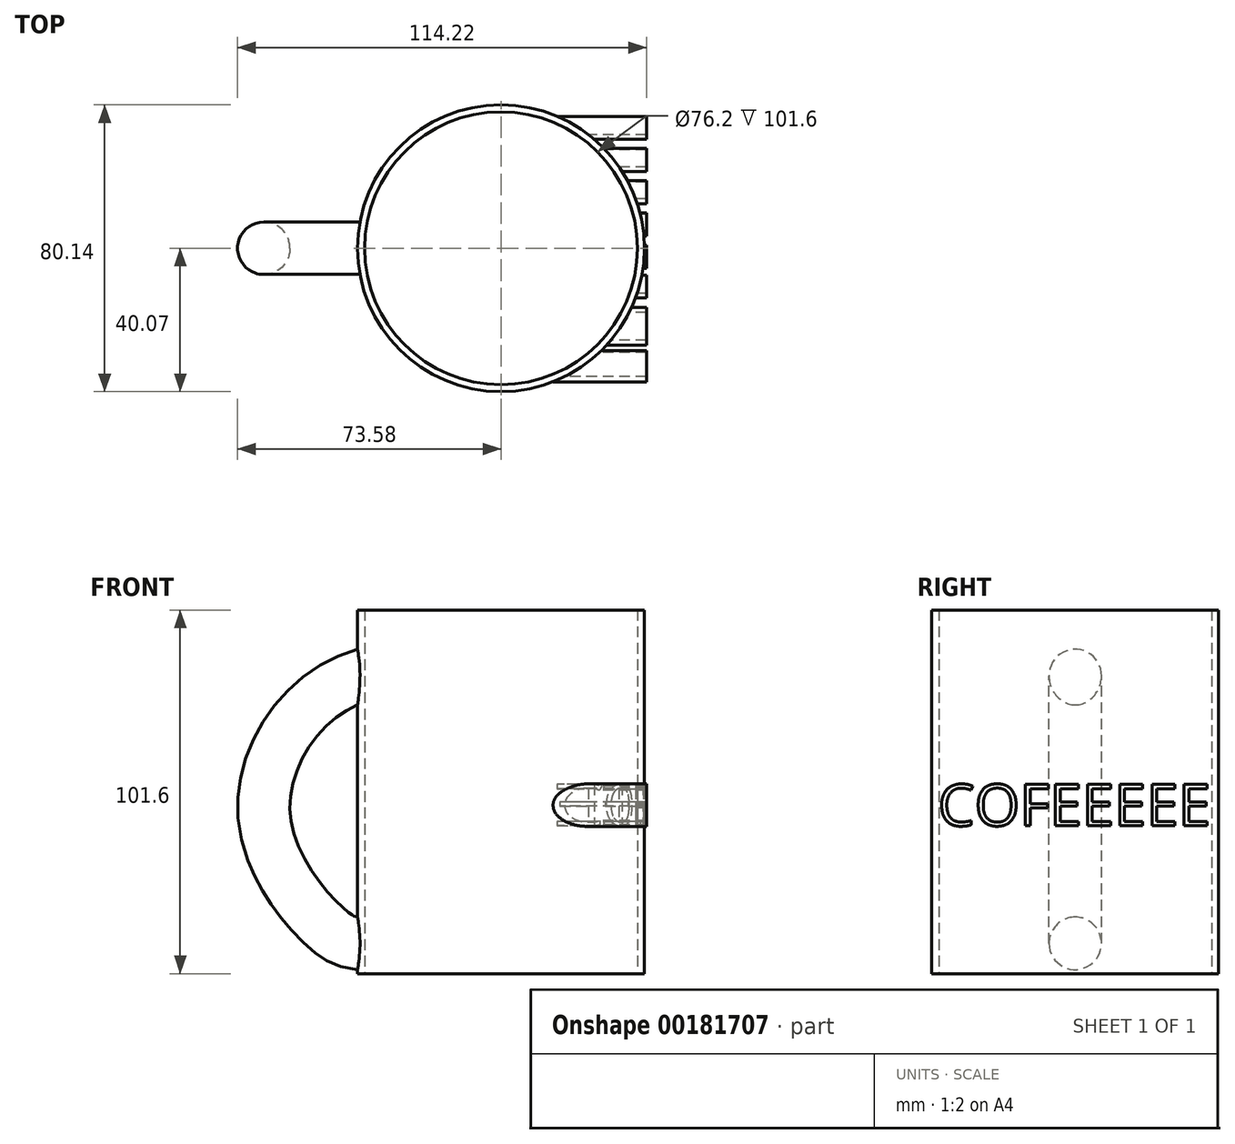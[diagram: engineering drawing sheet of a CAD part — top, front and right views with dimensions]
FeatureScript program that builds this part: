
annotation { "Feature Type Name" : "Feature", "Feature Type Description" : "" }
export const myFeature = defineFeature(function(context is Context, id is Id, definition is map)
    precondition{}
    {
        {
            var Q0;
            Q0=qCreatedBy(makeId("Top.planeOp"),FACE);
            var sketch = newSketch(context, id + "F0", { "sketchPlane" : qUnion([Q0])});
            skCircle(sketch, "E0", {"center": v(0, 0) * mm, "radius": 40.07 * mm});
            skSolve(sketch);
        }
        {
            var Q0;
            Q0 = qSketchRegion(id + "F0", true);
            extrude(context, id + "F1", {"entities" : qUnion([Q0]), "depth" : 101.6 * mm});
        }
        {
            var Q0;
            Q0=qCreatedBy(makeId("Right.planeOp"),FACE);
            var sketch = newSketch(context, id + "F2", { "sketchPlane" : qUnion([Q0])});
            skCircle(sketch, "E1", {"center": v(0, 84.76) * mm, "radius": 7.33 * mm});
            skSolve(sketch);
        }
        {
            var Q0;
            Q0=qCreatedBy(makeId("Front.planeOp"),FACE);
            var sketch = newSketch(context, id + "F3", { "sketchPlane" : qUnion([Q0])});
            skFitSpline(sketch, "E2", {"points": [v(0, 84.72) * mm, v(-47.14, 79.6) * mm, v(-66, 42.7) * mm, v(-47.14, 11.45) * mm, v(-9.6, 9.51) * mm], "startDerivative": vector(-191.11, 15.43) * mm, "endDerivative": vector(359.14, 4.67) * mm});
            skSolve(sketch);
        }
        {
            var Q0;
            Q0 = qSketchRegion(id + "F2", true);
            var Q1;
            Q1 = qConstructionFilter(qBodyType(qCreatedBy(id + "F3" ,EDGE), BodyType.WIRE), ConstructionObject.NO);
            sweep(context, id + "F4", {"operationType" : NewBodyOperationType.ADD, "profiles" : qUnion([Q0]), "path" : qUnion([Q1])});
        }
        {
            var Q0;
            Q0=qCreatedBy(makeId("Right.planeOp"),FACE);
            var sketch = newSketch(context, id + "F5", { "sketchPlane" : qUnion([Q0])});
            skText(sketch, "E3", { "text": "COFEEEEE", "fontName": "OpenSans-Regular.ttf"});
            const initialGuessF5  = {"E3": [-0.03832, 0.04131, 1, 0, 0.01165]};
            skSetInitialGuess(sketch, initialGuessF5);
            skSolve(sketch);
        }
        {
            var Q0;
            Q0 = qSketchRegion(id + "F5", true);
            extrude(context, id + "F6", {"entities" : qUnion([Q0]), "operationType" : NewBodyOperationType.ADD, "depth" : 40.64 * mm});
        }
        {
            var Q0;
            Q0=qCreatedBy(makeId("Top.planeOp"),FACE);
            var sketch = newSketch(context, id + "F7", { "sketchPlane" : qUnion([Q0])});
            skCircle(sketch, "E4", {"center": v(0, 0) * mm, "radius": 38.1 * mm});
            skSolve(sketch);
        }
        {
            var Q0;
            Q0 = qSketchRegion(id + "F7", true);
            extrude(context, id + "F8", {"entities" : qUnion([Q0]), "operationType" : NewBodyOperationType.REMOVE, "depth" : 134.37 * mm});
        }
    });
